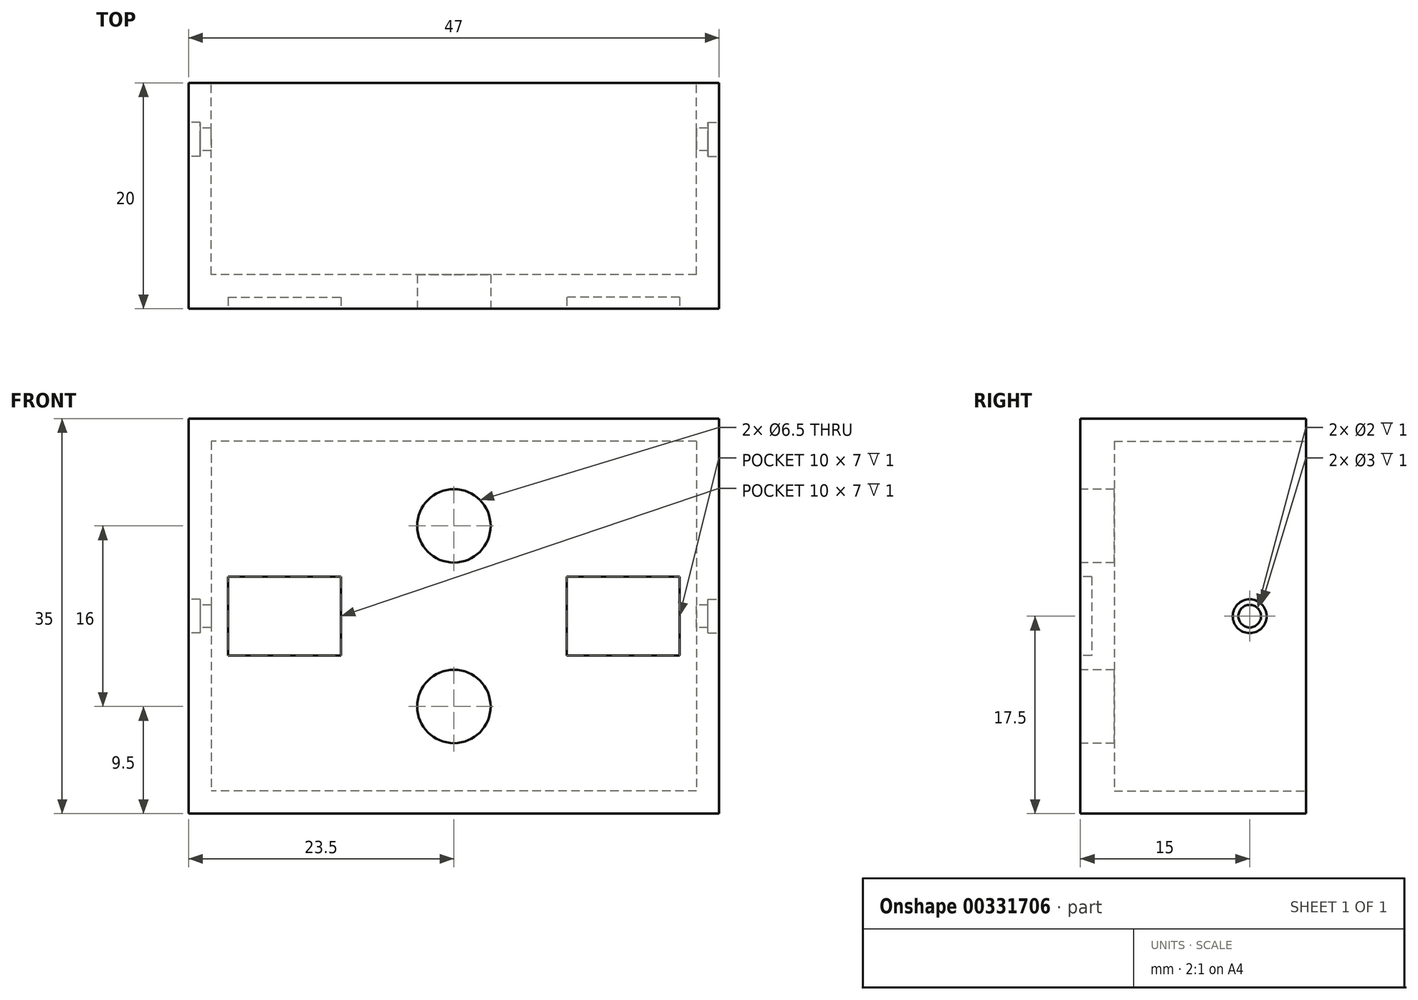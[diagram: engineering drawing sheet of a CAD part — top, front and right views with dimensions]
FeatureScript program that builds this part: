
annotation { "Feature Type Name" : "Feature", "Feature Type Description" : "" }
export const myFeature = defineFeature(function(context is Context, id is Id, definition is map)
    precondition{}
    {
        {
            var Q0;
            Q0=qCreatedBy(makeId("Front.planeOp"),FACE);
            var sketch = newSketch(context, id + "F0", { "sketchPlane" : qUnion([Q0])});
            skLineSegment(sketch, "E0.bottom", {"start": v(23.5, 17.5) * mm, "end": v(-23.5, 17.5) * mm});
            skLineSegment(sketch, "E0.top", {"start": v(23.5, -17.5) * mm, "end": v(-23.5, -17.5) * mm});
            skLineSegment(sketch, "E0.left", {"start": v(23.5, 17.5) * mm, "end": v(23.5, -17.5) * mm});
            skLineSegment(sketch, "E0.right", {"start": v(-23.5, 17.5) * mm, "end": v(-23.5, -17.5) * mm});
            skPoint(sketch, "E0.middle", {"position": v(0, 0) * mm});
            skSolve(sketch);
        }
        {
            var Q0;
            Q0=makeQuery(id+"F0.imprint","IMPRINT",FACE,{"disambiguationData":[TD([[makeQuery(id+"F0.imprint","IMPRINT",EDGE,{"derivedFrom":sQuery(id+"F0.wireOp",EDGE,"E0.bottom")}),1.0]])]});
            extrude(context, id + "F1", {"entities" : qUnion([Q0]), "depth" : 19 * mm});
        }
        {
            var Q0;
            Q0=makeQuery(id+"F1.opExtrude","CAP_FACE",FACE,{"disambiguationData":[OSD([sQuery(id+"F0.wireOp",EDGE,"E0.bottom"),sQuery(id+"F0.wireOp",EDGE,"E0.top"),sQuery(id+"F0.wireOp",EDGE,"E0.left"),sQuery(id+"F0.wireOp",EDGE,"E0.right")])],"isStart":true});
            shell(context, id + "F2", {"entities" : qUnion([Q0]), "thickness" : 2 * mm});
        }
        {
            var Q0;
            Q0=makeQuery(id+"F1.opExtrude","CAP_FACE",FACE,{"disambiguationData":[OSD([sQuery(id+"F0.wireOp",EDGE,"E0.bottom"),sQuery(id+"F0.wireOp",EDGE,"E0.top"),sQuery(id+"F0.wireOp",EDGE,"E0.left"),sQuery(id+"F0.wireOp",EDGE,"E0.right")])],"isStart":false});
            var sketch = newSketch(context, id + "F3", { "sketchPlane" : qUnion([Q0])});
            skCircle(sketch, "E1", {"center": v(0, 8) * mm, "radius": 3.25 * mm});
            skCircle(sketch, "E2", {"center": v(0, -8) * mm, "radius": 3.25 * mm});
            skSolve(sketch);
        }
        {
            var Q0;
            Q0 = qSketchRegion(id + "F3", true);
            extrude(context, id + "F4", {"entities" : qUnion([Q0]), "operationType" : NewBodyOperationType.REMOVE, "endBound" : BoundingType.THROUGH_ALL, "oppositeDirection" : true, "depth" : 25 * mm});
        }
        {
            var Q0;
            Q0=makeQuery(id+"F1.opExtrude","CAP_FACE",FACE,{"disambiguationData":[OSD([sQuery(id+"F0.wireOp",EDGE,"E0.bottom"),sQuery(id+"F0.wireOp",EDGE,"E0.top"),sQuery(id+"F0.wireOp",EDGE,"E0.left"),sQuery(id+"F0.wireOp",EDGE,"E0.right")])],"isStart":false});
            extrude(context, id + "F5", {"entities" : qUnion([Q0]), "operationType" : NewBodyOperationType.ADD, "depth" : 1 * mm});
        }
        {
            var Q0;
            Q0=makeQuery(id+"F5.opExtrude","CAP_FACE",FACE,{"disambiguationData":[OSD([sQuery(id+"F0.wireOp",EDGE,"E0.bottom"),sQuery(id+"F0.wireOp",EDGE,"E0.top"),sQuery(id+"F0.wireOp",EDGE,"E0.left"),sQuery(id+"F0.wireOp",EDGE,"E0.right")])],"isStart":false});
            var sketch = newSketch(context, id + "F6", { "sketchPlane" : qUnion([Q0])});
            skSolve(sketch);
        }
        {
            var Q0;
            {var subQ0=sQuery(id+"F0.wireOp",EDGE,"E0.right");Q0=makeQuery(id+"F5.boolean.opBoolean","MERGE",FACE,{"derivedFrom":[makeQuery(id+"F1.opExtrude","SWEPT_FACE",FACE,{"disambiguationData":[OSD([subQ0])]}),makeQuery(id+"F5.opExtrude","SWEPT_FACE",FACE,{"disambiguationData":[OSD([subQ0])]})]});}
            var sketch = newSketch(context, id + "F7", { "sketchPlane" : qUnion([Q0])});
            skCircle(sketch, "E3", {"center": v(5, 0) * mm, "radius": 1 * mm});
            skPoint(sketch, "E3.centerSnap0", {"position": v(0, 0) * mm});
            skSolve(sketch);
        }
        {
            var Q0;
            Q0=makeQuery(id+"F7.imprint","IMPRINT",FACE,{"disambiguationData":[TD([[makeQuery(id+"F7.imprint","IMPRINT",EDGE,{"derivedFrom":sQuery(id+"F7.wireOp",EDGE,"E3")}),1.0]])]});
            extrude(context, id + "F8", {"entities" : qUnion([Q0]), "operationType" : NewBodyOperationType.REMOVE, "endBound" : BoundingType.THROUGH_ALL, "oppositeDirection" : true, "depth" : 25 * mm});
        }
        {
            var Q0;
            {var subQ0=sQuery(id+"F0.wireOp",EDGE,"E0.right");Q0=makeQuery(id+"F5.boolean.opBoolean","MERGE",FACE,{"derivedFrom":[makeQuery(id+"F1.opExtrude","SWEPT_FACE",FACE,{"disambiguationData":[OSD([subQ0])]}),makeQuery(id+"F5.opExtrude","SWEPT_FACE",FACE,{"disambiguationData":[OSD([subQ0])]})]});}
            var sketch = newSketch(context, id + "F9", { "sketchPlane" : qUnion([Q0])});
            skCircle(sketch, "E4", {"center": v(5, 0) * mm, "radius": 1.5 * mm});
            skSolve(sketch);
        }
        {
            var Q0;
            Q0 = qSketchRegion(id + "F9", true);
            extrude(context, id + "F10", {"entities" : qUnion([Q0]), "operationType" : NewBodyOperationType.REMOVE, "oppositeDirection" : true, "depth" : 1 * mm});
        }
        {
            var Q0;
            {var subQ0=sQuery(id+"F0.wireOp",EDGE,"E0.left");Q0=makeQuery(id+"F5.boolean.opBoolean","MERGE",FACE,{"derivedFrom":[makeQuery(id+"F1.opExtrude","SWEPT_FACE",FACE,{"disambiguationData":[OSD([subQ0])]}),makeQuery(id+"F5.opExtrude","SWEPT_FACE",FACE,{"disambiguationData":[OSD([subQ0])]})]});}
            var sketch = newSketch(context, id + "F11", { "sketchPlane" : qUnion([Q0])});
            skCircle(sketch, "E5", {"center": v(-5, 0) * mm, "radius": 1.5 * mm});
            skSolve(sketch);
        }
        {
            var Q0;
            Q0 = qSketchRegion(id + "F11", true);
            extrude(context, id + "F12", {"entities" : qUnion([Q0]), "operationType" : NewBodyOperationType.REMOVE, "oppositeDirection" : true, "depth" : 1 * mm});
        }
        {
            var Q0;
            Q0=makeQuery(id+"F6.imprint","IMPRINT",FACE,{"disambiguationData":[TD([[makeQuery(id+"F6.imprint","IMPRINT",EDGE,{"derivedFrom":makeQuery(id+"F5.opExtrude","CAP_EDGE",EDGE,{"disambiguationData":[OSD([sQuery(id+"F0.wireOp",EDGE,"E0.bottom")])],"isStart":false})}),1.0]])]});
            var sketch = newSketch(context, id + "F13", { "sketchPlane" : qUnion([Q0])});
            skLineSegment(sketch, "E6.bottom", {"start": v(-20, 3.5) * mm, "end": v(-10, 3.5) * mm});
            skLineSegment(sketch, "E6.top", {"start": v(-20, -3.5) * mm, "end": v(-10, -3.5) * mm});
            skLineSegment(sketch, "E6.left", {"start": v(-20, 3.5) * mm, "end": v(-20, -3.5) * mm});
            skLineSegment(sketch, "E6.right", {"start": v(-10, 3.5) * mm, "end": v(-10, -3.5) * mm});
            skLineSegment(sketch, "E7", {"start": v(0, 0) * mm, "end": v(0, 13.9) * mm, "construction": true});
            skLineSegment(sketch, "E8.MirrorCS", {"start": v(10, 3.5) * mm, "end": v(10, -3.5) * mm});
            skLineSegment(sketch, "E9.MirrorCS", {"start": v(20, 3.5) * mm, "end": v(10, 3.5) * mm});
            skLineSegment(sketch, "E10.MirrorCS", {"start": v(20, 3.5) * mm, "end": v(20, -3.5) * mm});
            skLineSegment(sketch, "E11.MirrorCS", {"start": v(20, -3.5) * mm, "end": v(10, -3.5) * mm});
            skSolve(sketch);
        }
        {
            var Q0;
            Q0 = qSketchRegion(id + "F13", true);
            extrude(context, id + "F14", {"entities" : qUnion([Q0]), "operationType" : NewBodyOperationType.REMOVE, "oppositeDirection" : true, "depth" : 1 * mm});
        }
    });
